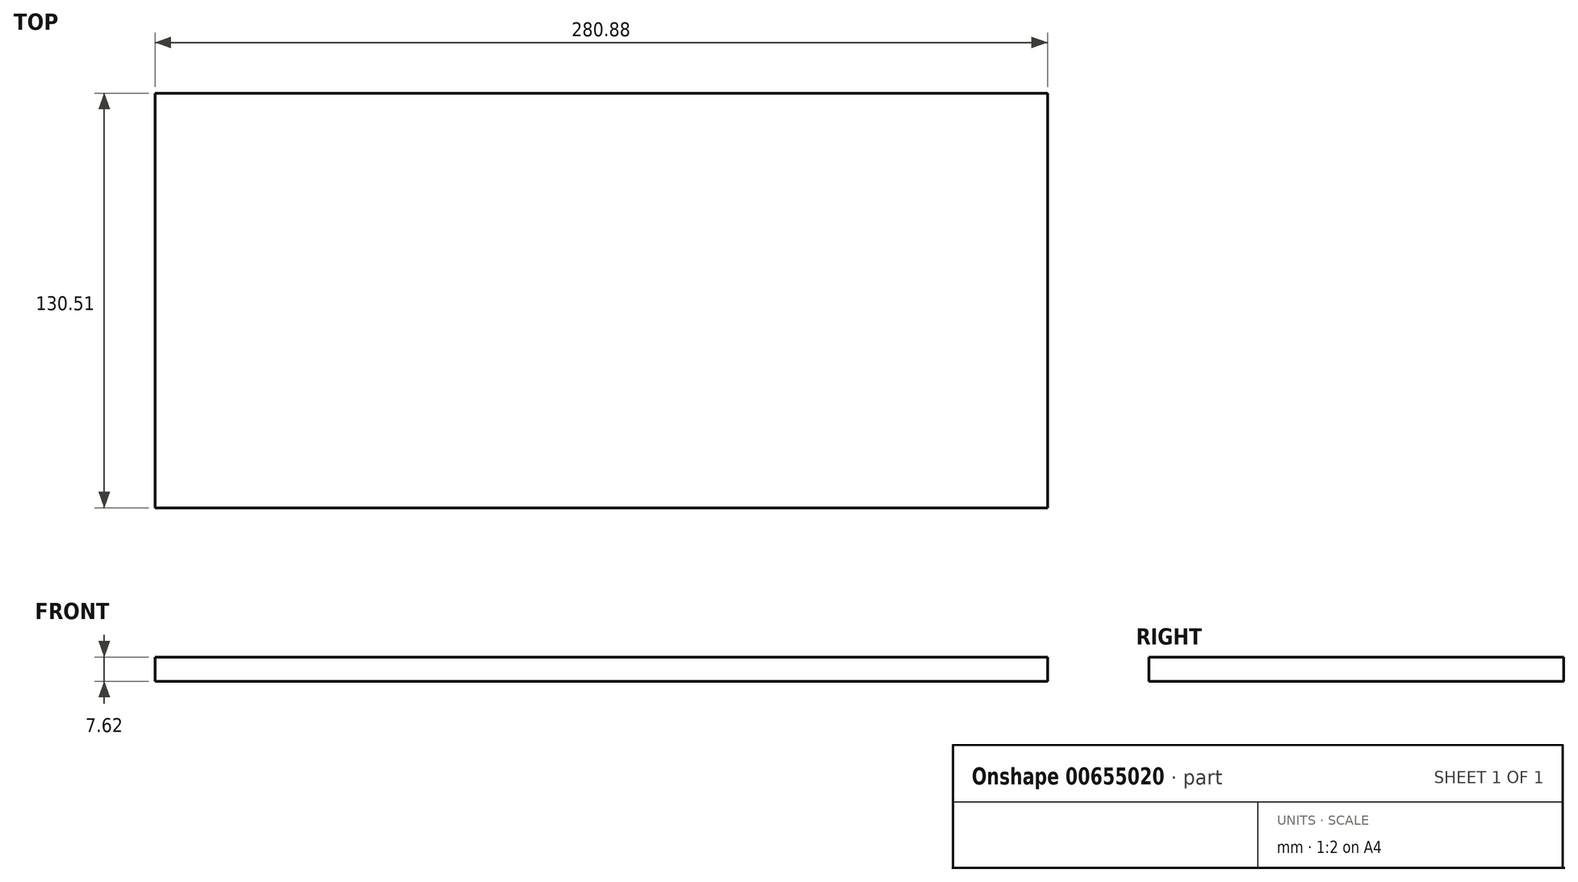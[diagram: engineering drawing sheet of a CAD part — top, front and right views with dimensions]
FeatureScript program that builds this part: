
annotation { "Feature Type Name" : "Feature", "Feature Type Description" : "" }
export const myFeature = defineFeature(function(context is Context, id is Id, definition is map)
    precondition{}
    {
        {
            var Q0;
            Q0=qCreatedBy(makeId("Top.planeOp"),FACE);
            var sketch = newSketch(context, id + "F0", { "sketchPlane" : qUnion([Q0])});
            skLineSegment(sketch, "E0.bottom", {"start": v(-142.49, 64.61) * mm, "end": v(138.39, 64.61) * mm});
            skLineSegment(sketch, "E0.top", {"start": v(-142.49, -65.9) * mm, "end": v(138.39, -65.9) * mm});
            skLineSegment(sketch, "E0.left", {"start": v(-142.49, 64.61) * mm, "end": v(-142.49, -65.9) * mm});
            skLineSegment(sketch, "E0.right", {"start": v(138.39, 64.61) * mm, "end": v(138.39, -65.9) * mm});
            skSolve(sketch);
        }
        {
            var Q0;
            Q0 = qSketchRegion(id + "F0", true);
            extrude(context, id + "F1", {"entities" : qUnion([Q0]), "depth" : 7.62 * mm, "offsetDistance" : 25.4 * mm});
        }
    });
